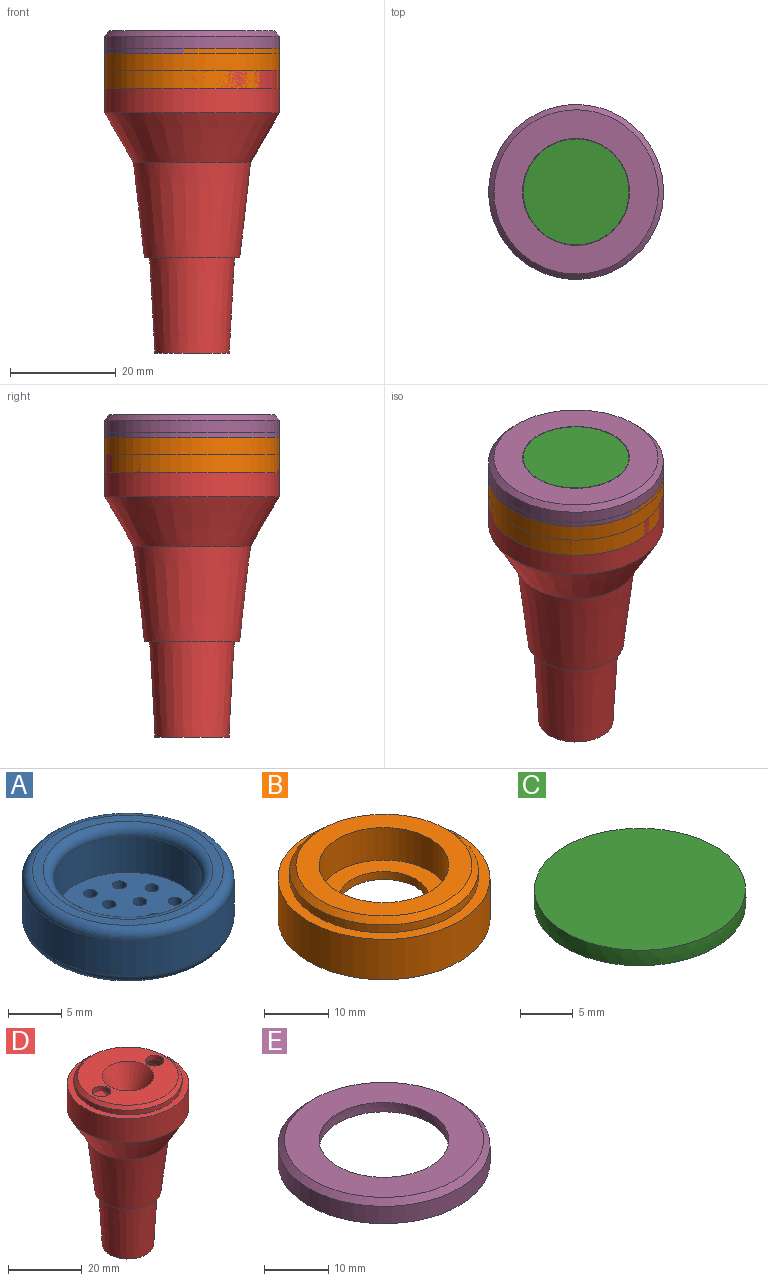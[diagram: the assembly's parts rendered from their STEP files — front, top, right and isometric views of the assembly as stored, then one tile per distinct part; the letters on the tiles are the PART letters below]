
ASSEMBLY  parts=5 mates=4
PART A: 23 faces, bbox 21.6x21.6x6.2 mm
  f0: plane 18x18mm, normal (0,0,-1), area 234.6mm2, adj f1,f8,f9,f10,f11,f12,f13,f14
  f1: torus R=9mm, axis (0,0,-1), area 95.1mm2, adj f0,f2
  f2: cylinder r=10mm len=20mm, axis (0,0,-1), area 262.6mm2, adj f1,f3
  f3: torus R=9mm, axis (0,0,-1), area 95.1mm2, adj f2,f4
  f4: plane 18x18mm, normal (0,0,1), area 53.4mm2, adj f3,f5
  f5: torus R=8mm, axis (0,0,-1), area 72.7mm2, adj f4,f6
  f6: cylinder r=7mm len=14mm, axis (0,0,-1), area 183.8mm2, adj f5,f7
  f7: plane 14x14mm, normal (0,0,1), area 134mm2, adj f6,f8,f9,f10,f11,f12,f13,f14
  f8: cylinder r=0.65mm len=1.3mm, axis (0,0,1), area 4.1mm2, adj f0,f7
  f9: cylinder r=0.65mm len=1.3mm, axis (0,0,1), area 4.1mm2, adj f0,f7
  f10: cylinder r=0.65mm len=1.3mm, axis (0,0,1), area 4.1mm2, adj f0,f7
  f11: cylinder r=0.65mm len=1.3mm, axis (0,0,1), area 4.1mm2, adj f0,f7
  f12: cylinder r=0.65mm len=1.3mm, axis (0,0,1), area 4.1mm2, adj f0,f7
  f13: cylinder r=0.65mm len=1.3mm, axis (0,0,1), area 4.1mm2, adj f0,f7
  f14: cylinder r=0.65mm len=1.3mm, axis (0,0,1), area 4.1mm2, adj f0,f7
  f15: cylinder r=0.65mm len=1.3mm, axis (0,0,1), area 4.1mm2, adj f0,f7
  f16: cylinder r=0.65mm len=1.3mm, axis (0,0,1), area 4.1mm2, adj f0,f7
  f17: cylinder r=0.65mm len=1.3mm, axis (0,0,1), area 4.1mm2, adj f0,f7
  f18: cylinder r=0.65mm len=1.3mm, axis (0,0,1), area 4.1mm2, adj f0,f7
  f19: cylinder r=0.65mm len=1.3mm, axis (0,0,1), area 4.1mm2, adj f0,f7
  f20: cylinder r=0.65mm len=1.3mm, axis (0,0,1), area 4.1mm2, adj f0,f7
  f21: cylinder r=0.65mm len=1.3mm, axis (0,0,1), area 4.1mm2, adj f0,f7
  f22: cylinder r=0.65mm len=1.3mm, axis (0,0,1), area 4.1mm2, adj f0,f7
PART B: 12 faces, bbox 33x33x10.2 mm
  f0: plane 27.4x27.4mm, normal (0,0,-1), area 435.7mm2, adj f9,f10
  f1: cylinder r=14.7mm len=29.4mm, axis (0,0,-1), area 138.5mm2, adj f2,f10
  f2: plane 33x33mm, normal (0,0,-1), area 176.4mm2, adj f1,f3
  f3: cylinder r=16.5mm len=33mm, axis (0,0,-1), area 796.2mm2, adj f2,f4
  f4: plane 33x33mm, normal (0,0,1), area 176.4mm2, adj f3,f5
  f5: cylinder r=14.7mm len=29.4mm, axis (0,0,-1), area 138.5mm2, adj f4,f11
  f6: plane 27.4x27.4mm, normal (0,0,1), area 269.2mm2, adj f7,f11
  f7: cylinder r=10.1mm len=20.2mm, axis (0,0,-1), area 392.2mm2, adj f6,f8
  f8: plane 20.2x20.2mm, normal (0,0,1), area 166.5mm2, adj f7,f9
  f9: cylinder r=7mm len=14mm, axis (0,0,-1), area 66mm2, adj f0,f8
  f10: cone r=13.7mm half-angle=45deg, axis (0,0,-1), area 126.2mm2, adj f0,f1
  f11: cone r=14.7mm half-angle=45deg, axis (0,0,-1), area 126.2mm2, adj f5,f6
PART C: 3 faces, bbox 20.1x20.1x1.8 mm
  f0: plane 20x20mm, normal (0,0,1), area 314.2mm2, adj f2
  f1: plane 20x20mm, normal (0,0,-1), area 314.2mm2, adj f2
  f2: sphere r=10.04mm, area 113.6mm2, adj f0,f1
PART D: 25 faces, bbox 33x33x55.9 mm
  f0: cone r=3mm half-angle=27.6deg, axis (0,0,1), area 361.7mm2, adj f2,f3,f11,f12
  f1: plane 11.16x11.16mm, normal (0,0,1), area 69.6mm2, adj f2,f10
  f2: cylinder r=3mm len=43.52mm, axis (0,0,-1), area 820.4mm2, adj f0,f1
  f3: plane 26.4x26.4mm, normal (0,0,-1), area 312mm2, adj f0,f4,f11,f12
  f4: cylinder r=13.2mm len=26.4mm, axis (0,0,-1), area 207.3mm2, adj f3,f5
  f5: plane 30x30mm, normal (0,0,-1), area 159.5mm2, adj f4,f6
  f6: cylinder r=15mm len=30mm, axis (0,0,-1), area 574.6mm2, adj f5,f7
  f7: cone r=15mm half-angle=30.1deg, axis (0,0,1), area 831.9mm2, adj f6,f8
  f8: cone r=7.66mm half-angle=6.5deg, axis (0,0,1), area 927.1mm2, adj f7,f9
  f9: plane 15.32x15.32mm, normal (0,0,1), area 48.4mm2, adj f8,f10
  f10: cone r=5.58mm half-angle=3.2deg, axis (0,0,1), area 688.8mm2, adj f1,f9
  f11: cylinder r=2.5mm len=5mm, axis (0,0,1), area 23.9mm2, adj f0,f3,f23
  f12: cylinder r=2.5mm len=5mm, axis (0,0,1), area 23.9mm2, adj f0,f3,f23
  f13: cone r=1.5mm half-angle=27.6deg, axis (0,0,1), area 316.5mm2, adj f14,f23
  f14: cylinder r=1.5mm len=45.39mm, axis (0,0,-1), area 427.8mm2, adj f13,f15
  f15: plane 14x14mm, normal (0,0,-1), area 146.9mm2, adj f14,f16
  f16: cone r=7mm half-angle=3.2deg, axis (0,0,1), area 849.5mm2, adj f15,f17
  f17: plane 18x18mm, normal (0,0,-1), area 53.4mm2, adj f16,f18
  f18: cone r=9mm half-angle=6.5deg, axis (0,0,1), area 1141.7mm2, adj f17,f19
  f19: cone r=16.5mm half-angle=30.1deg, axis (0,0,1), area 939.6mm2, adj f18,f20
  f20: cylinder r=16.5mm len=33mm, axis (0,0,-1), area 829.4mm2, adj f19,f21
  f21: plane 33x33mm, normal (0,0,1), area 176.4mm2, adj f20,f22
  f22: cylinder r=14.7mm len=29.4mm, axis (0,0,-1), area 138.5mm2, adj f21,f24
  f23: plane 27.4x27.4mm, normal (0,0,1), area 396.4mm2, adj f11,f12,f13,f24
  f24: cone r=14.7mm half-angle=45deg, axis (0,0,-1), area 126.2mm2, adj f22,f23
PART E: 8 faces, bbox 33x33x4.3 mm
  f0: cylinder r=16.5mm len=33mm, axis (0,0,-1), area 342.1mm2, adj f5,f6
  f1: plane 31x31mm, normal (0,0,1), area 434.3mm2, adj f2,f6
  f2: sphere r=10.14mm, area 114.7mm2, adj f1,f3
  f3: plane 29.4x29.4mm, normal (0,0,-1), area 358.4mm2, adj f2,f4
  f4: cylinder r=14.7mm len=29.4mm, axis (0,0,-1), area 138.5mm2, adj f3,f7
  f5: plane 33x33mm, normal (0,0,-1), area 80.9mm2, adj f0,f7
  f6: cone r=16.5mm half-angle=45deg, axis (0,0,-1), area 142.2mm2, adj f0,f1
  f7: cone r=14.7mm half-angle=45deg, axis (0,0,-1), area 135.1mm2, adj f4,f5
PLACE A t=(37.08,24.4,-27.64)mm
PLACE B t=(37.08,24.4,-25.74)mm
PLACE C t=(37.08,24.4,-35.41)mm
PLACE D t=(37.08,24.4,-3.93)mm
PLACE E t=(37.08,24.4,-35.41)mm
MATE slider A.f1 <-> B.f1  axis (0,0,-1) through (37.08,24.4,7.63)mm
MATE cylindrical C.f2 <-> E.f0  axis (0,0,1) through (37.08,24.4,10.62)mm
MATE slider D.f0 <-> B.f1  axis (0,0,-1) through (37.08,24.4,4.82)mm
MATE slider E.f0 <-> B.f1  axis (0,0,-1) through (37.08,24.4,8.97)mm
